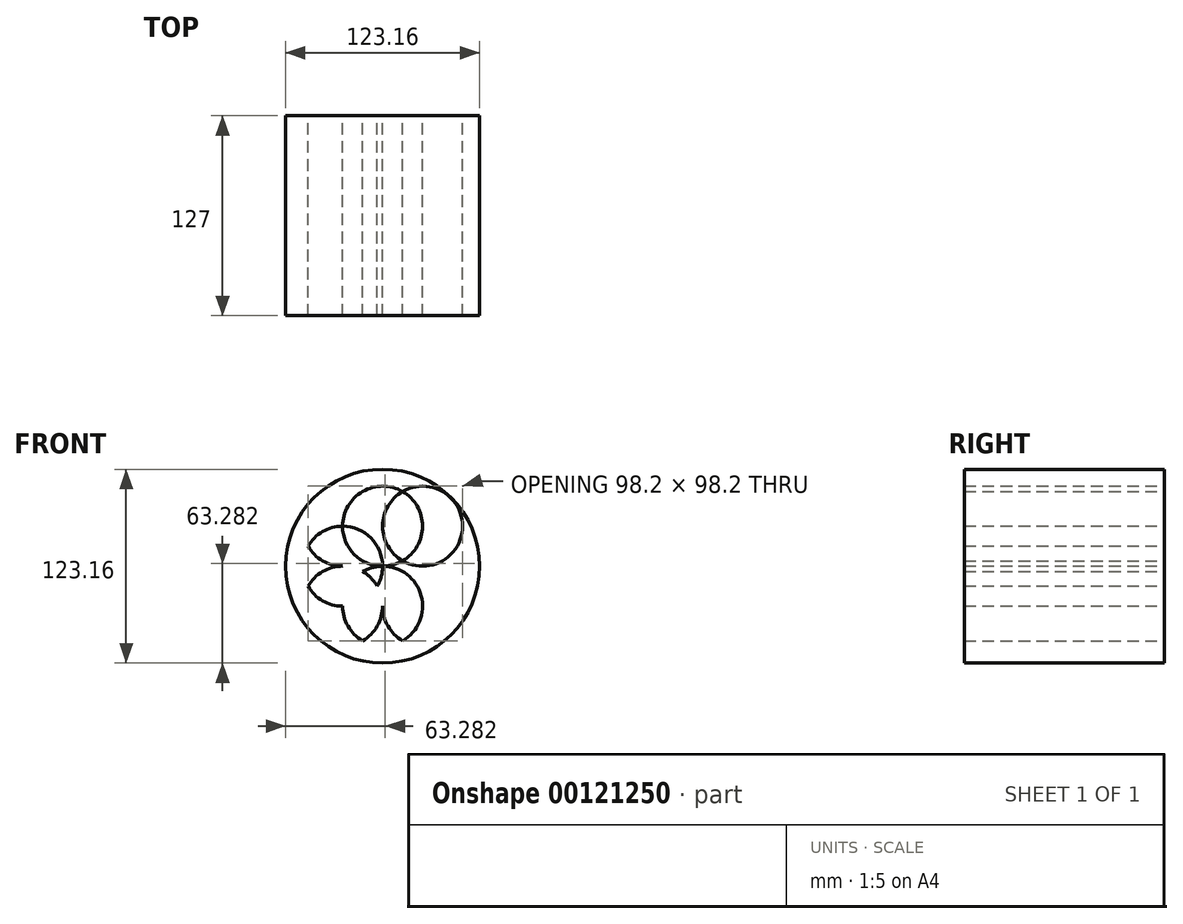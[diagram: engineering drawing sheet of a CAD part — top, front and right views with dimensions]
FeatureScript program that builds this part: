
annotation { "Feature Type Name" : "Feature", "Feature Type Description" : "" }
export const myFeature = defineFeature(function(context is Context, id is Id, definition is map)
    precondition{}
    {
        {
            var Q0;
            Q0=qCreatedBy(makeId("Front.planeOp"),FACE);
            var sketch = newSketch(context, id + "F0", { "sketchPlane" : qUnion([Q0])});
            skCircle(sketch, "E0", {"center": v(0, 0) * mm, "radius": 25.4 * mm});
            skCircle(sketch, "E1", {"center": v(0, 25.4) * mm, "radius": 25.4 * mm});
            skCircle(sketch, "E2", {"center": v(0, -25.4) * mm, "radius": 25.4 * mm});
            skCircle(sketch, "E3", {"center": v(25.4, 0) * mm, "radius": 25.4 * mm});
            skCircle(sketch, "E4", {"center": v(-25.4, 0) * mm, "radius": 25.4 * mm});
            skCircle(sketch, "E5", {"center": v(25.4, 25.4) * mm, "radius": 25.4 * mm});
            skCircle(sketch, "E6", {"center": v(-25.4, 25.4) * mm, "radius": 25.4 * mm});
            skCircle(sketch, "E7", {"center": v(-25.4, -25.4) * mm, "radius": 25.4 * mm});
            skCircle(sketch, "E8", {"center": v(25.4, -25.4) * mm, "radius": 25.4 * mm});
            skCircle(sketch, "E9", {"center": v(0, 0) * mm, "radius": 61.58 * mm});
            skSolve(sketch);
        }
        {
            var Q0;
            {var subQ0=sQuery(id+"F0.wireOp",EDGE,"E6");var subQ1=sQuery(id+"F0.wireOp",EDGE,"E1");var subQ2=makeQuery(id+"F0.imprint","INTERSECT",VERTEX,{"disambiguationData":[OD(1.0)],"derivedFrom":[subQ1,subQ0]});Q0=makeQuery(id+"F0.imprint","IMPRINT",FACE,{"disambiguationData":[TD([[makeQuery(id+"F0.imprint","IMPRINT",EDGE,{"disambiguationData":[TD([[subQ2,-1.0]])],"derivedFrom":subQ0}),-1.0]])]});}
            var Q1;
            {var subQ0=sQuery(id+"F0.wireOp",EDGE,"E4");var subQ1=sQuery(id+"F0.wireOp",EDGE,"E0");var subQ2=makeQuery(id+"F0.imprint","INTERSECT",VERTEX,{"disambiguationData":[OD(0.0)],"derivedFrom":[subQ1,subQ0]});Q1=makeQuery(id+"F0.imprint","IMPRINT",FACE,{"disambiguationData":[TD([[makeQuery(id+"F0.imprint","IMPRINT",EDGE,{"disambiguationData":[TD([[subQ2,-1.0]])],"derivedFrom":subQ1}),1.0]])]});}
            var Q2;
            {var subQ0=sQuery(id+"F0.wireOp",EDGE,"E4");var subQ1=sQuery(id+"F0.wireOp",EDGE,"E0");var subQ2=makeQuery(id+"F0.imprint","INTERSECT",VERTEX,{"disambiguationData":[OD(0.0)],"derivedFrom":[subQ1,subQ0]});Q2=makeQuery(id+"F0.imprint","IMPRINT",FACE,{"disambiguationData":[TD([[makeQuery(id+"F0.imprint","IMPRINT",EDGE,{"disambiguationData":[TD([[subQ2,-1.0]])],"derivedFrom":subQ1}),-1.0]])]});}
            var Q3;
            {var subQ0=sQuery(id+"F0.wireOp",EDGE,"E7");var subQ1=sQuery(id+"F0.wireOp",EDGE,"E2");var subQ2=makeQuery(id+"F0.imprint","INTERSECT",VERTEX,{"disambiguationData":[OD(0.0)],"derivedFrom":[subQ1,subQ0]});Q3=makeQuery(id+"F0.imprint","IMPRINT",FACE,{"disambiguationData":[TD([[makeQuery(id+"F0.imprint","IMPRINT",EDGE,{"disambiguationData":[TD([[subQ2,1.0]])],"derivedFrom":subQ0}),-1.0]])]});}
            var Q4;
            {var subQ0=sQuery(id+"F0.wireOp",EDGE,"E2");var subQ1=sQuery(id+"F0.wireOp",EDGE,"E0");var subQ2=makeQuery(id+"F0.imprint","INTERSECT",VERTEX,{"disambiguationData":[OD(0.0)],"derivedFrom":[subQ1,subQ0]});Q4=makeQuery(id+"F0.imprint","IMPRINT",FACE,{"disambiguationData":[TD([[makeQuery(id+"F0.imprint","IMPRINT",EDGE,{"disambiguationData":[TD([[subQ2,-1.0]])],"derivedFrom":subQ1}),1.0]])]});}
            var Q5;
            {var subQ0=sQuery(id+"F0.wireOp",EDGE,"E2");var subQ1=sQuery(id+"F0.wireOp",EDGE,"E0");var subQ2=makeQuery(id+"F0.imprint","INTERSECT",VERTEX,{"disambiguationData":[OD(0.0)],"derivedFrom":[subQ1,subQ0]});Q5=makeQuery(id+"F0.imprint","IMPRINT",FACE,{"disambiguationData":[TD([[makeQuery(id+"F0.imprint","IMPRINT",EDGE,{"disambiguationData":[TD([[subQ2,-1.0]])],"derivedFrom":subQ1}),-1.0]])]});}
            var Q6;
            {var subQ0=sQuery(id+"F0.wireOp",EDGE,"E3");var subQ1=sQuery(id+"F0.wireOp",EDGE,"E0");var subQ2=makeQuery(id+"F0.imprint","INTERSECT",VERTEX,{"disambiguationData":[OD(1.0)],"derivedFrom":[subQ1,subQ0]});Q6=makeQuery(id+"F0.imprint","IMPRINT",FACE,{"disambiguationData":[TD([[makeQuery(id+"F0.imprint","IMPRINT",EDGE,{"disambiguationData":[TD([[subQ2,-1.0]])],"derivedFrom":subQ1}),1.0]])]});}
            var Q7;
            {var subQ0=sQuery(id+"F0.wireOp",EDGE,"E3");var subQ1=sQuery(id+"F0.wireOp",EDGE,"E0");var subQ2=makeQuery(id+"F0.imprint","INTERSECT",VERTEX,{"disambiguationData":[OD(1.0)],"derivedFrom":[subQ1,subQ0]});Q7=makeQuery(id+"F0.imprint","IMPRINT",FACE,{"disambiguationData":[TD([[makeQuery(id+"F0.imprint","IMPRINT",EDGE,{"disambiguationData":[TD([[subQ2,-1.0]])],"derivedFrom":subQ1}),-1.0]])]});}
            var Q8;
            {var subQ0=sQuery(id+"F0.wireOp",EDGE,"E8");var subQ1=sQuery(id+"F0.wireOp",EDGE,"E2");var subQ2=makeQuery(id+"F0.imprint","INTERSECT",VERTEX,{"disambiguationData":[OD(0.0)],"derivedFrom":[subQ1,subQ0]});Q8=makeQuery(id+"F0.imprint","IMPRINT",FACE,{"disambiguationData":[TD([[makeQuery(id+"F0.imprint","IMPRINT",EDGE,{"disambiguationData":[TD([[subQ2,-1.0]])],"derivedFrom":subQ0}),-1.0]])]});}
            var Q9;
            {var subQ0=sQuery(id+"F0.wireOp",EDGE,"E1");var subQ1=sQuery(id+"F0.wireOp",EDGE,"E0");var subQ2=makeQuery(id+"F0.imprint","INTERSECT",VERTEX,{"disambiguationData":[OD(0.0)],"derivedFrom":[subQ1,subQ0]});Q9=makeQuery(id+"F0.imprint","IMPRINT",FACE,{"disambiguationData":[TD([[makeQuery(id+"F0.imprint","IMPRINT",EDGE,{"disambiguationData":[TD([[subQ2,-1.0]])],"derivedFrom":subQ1}),1.0]])]});}
            var Q10;
            {var subQ0=sQuery(id+"F0.wireOp",EDGE,"E1");var subQ1=sQuery(id+"F0.wireOp",EDGE,"E0");var subQ2=makeQuery(id+"F0.imprint","INTERSECT",VERTEX,{"disambiguationData":[OD(0.0)],"derivedFrom":[subQ1,subQ0]});Q10=makeQuery(id+"F0.imprint","IMPRINT",FACE,{"disambiguationData":[TD([[makeQuery(id+"F0.imprint","IMPRINT",EDGE,{"disambiguationData":[TD([[subQ2,-1.0]])],"derivedFrom":subQ1}),-1.0]])]});}
            var Q11;
            {var subQ0=sQuery(id+"F0.wireOp",EDGE,"E5");var subQ1=sQuery(id+"F0.wireOp",EDGE,"E1");var subQ2=makeQuery(id+"F0.imprint","INTERSECT",VERTEX,{"disambiguationData":[OD(1.0)],"derivedFrom":[subQ1,subQ0]});Q11=makeQuery(id+"F0.imprint","IMPRINT",FACE,{"disambiguationData":[TD([[makeQuery(id+"F0.imprint","IMPRINT",EDGE,{"disambiguationData":[TD([[subQ2,1.0]])],"derivedFrom":subQ0}),-1.0]])]});}
            var Q12;
            {var subQ0=sQuery(id+"F0.wireOp",EDGE,"E6");var subQ1=sQuery(id+"F0.wireOp",EDGE,"E1");var subQ2=makeQuery(id+"F0.imprint","INTERSECT",VERTEX,{"disambiguationData":[OD(0.0)],"derivedFrom":[subQ1,subQ0]});Q12=makeQuery(id+"F0.imprint","IMPRINT",FACE,{"disambiguationData":[TD([[makeQuery(id+"F0.imprint","IMPRINT",EDGE,{"disambiguationData":[TD([[subQ2,-1.0]])],"derivedFrom":subQ1}),-1.0]])]});}
            var Q13;
            {var subQ0=sQuery(id+"F0.wireOp",EDGE,"E6");var subQ1=sQuery(id+"F0.wireOp",EDGE,"E4");var subQ2=makeQuery(id+"F0.imprint","INTERSECT",VERTEX,{"disambiguationData":[OD(1.0)],"derivedFrom":[subQ1,subQ0]});Q13=makeQuery(id+"F0.imprint","IMPRINT",FACE,{"disambiguationData":[TD([[makeQuery(id+"F0.imprint","IMPRINT",EDGE,{"disambiguationData":[TD([[subQ2,-1.0]])],"derivedFrom":subQ1}),1.0]])]});}
            var Q14;
            {var subQ0=sQuery(id+"F0.wireOp",EDGE,"E4");var subQ1=sQuery(id+"F0.wireOp",EDGE,"E2");var subQ2=makeQuery(id+"F0.imprint","INTERSECT",VERTEX,{"derivedFrom":[subQ1,subQ0]});Q14=makeQuery(id+"F0.imprint","IMPRINT",FACE,{"disambiguationData":[TD([[makeQuery(id+"F0.imprint","IMPRINT",EDGE,{"disambiguationData":[TD([[subQ2,-1.0]])],"derivedFrom":subQ1}),-1.0]])]});}
            var Q15;
            {var subQ0=sQuery(id+"F0.wireOp",EDGE,"E7");var subQ1=sQuery(id+"F0.wireOp",EDGE,"E2");var subQ2=makeQuery(id+"F0.imprint","INTERSECT",VERTEX,{"disambiguationData":[OD(1.0)],"derivedFrom":[subQ1,subQ0]});Q15=makeQuery(id+"F0.imprint","IMPRINT",FACE,{"disambiguationData":[TD([[makeQuery(id+"F0.imprint","IMPRINT",EDGE,{"disambiguationData":[TD([[subQ2,-1.0]])],"derivedFrom":subQ1}),1.0]])]});}
            var Q16;
            {var subQ0=sQuery(id+"F0.wireOp",EDGE,"E3");var subQ1=sQuery(id+"F0.wireOp",EDGE,"E2");var subQ2=makeQuery(id+"F0.imprint","INTERSECT",VERTEX,{"derivedFrom":[subQ1,subQ0]});Q16=makeQuery(id+"F0.imprint","IMPRINT",FACE,{"disambiguationData":[TD([[makeQuery(id+"F0.imprint","IMPRINT",EDGE,{"disambiguationData":[TD([[subQ2,1.0]])],"derivedFrom":subQ1}),-1.0]])]});}
            var Q17;
            {var subQ0=sQuery(id+"F0.wireOp",EDGE,"E5");var subQ1=sQuery(id+"F0.wireOp",EDGE,"E3");var subQ2=makeQuery(id+"F0.imprint","INTERSECT",VERTEX,{"disambiguationData":[OD(0.0)],"derivedFrom":[subQ1,subQ0]});Q17=makeQuery(id+"F0.imprint","IMPRINT",FACE,{"disambiguationData":[TD([[makeQuery(id+"F0.imprint","IMPRINT",EDGE,{"disambiguationData":[TD([[subQ2,1.0]])],"derivedFrom":subQ1}),1.0]])]});}
            var Q18;
            {var subQ0=sQuery(id+"F0.wireOp",EDGE,"E5");var subQ1=sQuery(id+"F0.wireOp",EDGE,"E1");var subQ2=makeQuery(id+"F0.imprint","INTERSECT",VERTEX,{"disambiguationData":[OD(0.0)],"derivedFrom":[subQ1,subQ0]});Q18=makeQuery(id+"F0.imprint","IMPRINT",FACE,{"disambiguationData":[TD([[makeQuery(id+"F0.imprint","IMPRINT",EDGE,{"disambiguationData":[TD([[subQ2,1.0]])],"derivedFrom":subQ1}),-1.0]])]});}
            var Q19;
            {var subQ0=sQuery(id+"F0.wireOp",EDGE,"E5");var subQ1=sQuery(id+"F0.wireOp",EDGE,"E1");var subQ2=makeQuery(id+"F0.imprint","INTERSECT",VERTEX,{"disambiguationData":[OD(0.0)],"derivedFrom":[subQ1,subQ0]});Q19=makeQuery(id+"F0.imprint","IMPRINT",FACE,{"disambiguationData":[TD([[makeQuery(id+"F0.imprint","IMPRINT",EDGE,{"disambiguationData":[TD([[subQ2,-1.0]])],"derivedFrom":subQ1}),1.0]])]});}
            extrude(context, id + "F1", {"entities" : qUnion([Q0, Q1, Q2, Q3, Q4, Q5, Q6, Q7, Q8, Q9, Q10, Q11, Q12, Q13, Q14, Q15, Q16, Q17, Q18, Q19]), "endBound" : BoundingType.SYMMETRIC, "depth" : 127 * mm});
        }
    });
